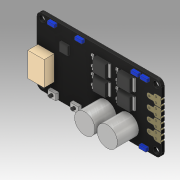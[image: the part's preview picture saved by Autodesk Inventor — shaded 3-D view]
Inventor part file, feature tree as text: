
AUTODESK INVENTOR PART (.ipt)
format: ipt  version: 2019.3 (Build 233278000, 278)  size: 836,096 bytes
history: native  units: mm
features: projected_geometry x23, extrude x14, sketch x14
ambient origin geometry x8: Origin, YZ Plane, XZ Plane, XY Plane, X Axis, Y Axis, Z Axis, Center Point
bodies: Solid1 (feature_tree)
feature tree (51):
  extrude  "Extrusion1"  Depth=33.0mm
  extrude  "Extrusion2"  Depth=3.0mm
  extrude  "Extrusion3"  Depth=28.0mm
  extrude  "Extrusion4"  Depth=10.0mm
  extrude  "Extrusion5"  Depth=21.0mm
  extrude  "Extrusion6"  Depth=10.5mm TaperAngle=0.0deg
  extrude  "Extrusion7"  Depth=6.0mm
  extrude  "Extrusion8"  Depth=4.5mm
  extrude  "Extrusion9"  Depth=2.1mm TaperAngle=0.0deg
  extrude  "Extrusion10"  Depth=0.6mm TaperAngle=0.0deg
  extrude  "Extrusion11"  Depth=2.5mm
  extrude  "Extrusion12"  Depth=3.5mm
  extrude  "Extrusion13"  Depth=5.5mm
  extrude  "Extrusion14"  Depth=0.25mm
  sketch  "Sketch1"  dims[d0=61.0mm d1=33.0mm]
  sketch  "Sketch2"  dims[d2=2.5mm d3=3.0mm]
  projected_geometry  "Projected Loop1"
  sketch  "Sketch3"  dims[d4=56.0mm d5=28.0mm]
  projected_geometry  "Projected Loop2"
  sketch  "Sketch4"  dims[d6=1.6mm d7=0.0mm d8=10.0mm]
  projected_geometry  "Projected Loop3"
  projected_geometry  "Projected Loop4"
  projected_geometry  "Projected Loop5"
  projected_geometry  "Projected Loop6"
  projected_geometry  "Projected Loop7"
  sketch  "Sketch5"  dims[d9=21.0mm d10=21.0mm]
  projected_geometry  "Projected Loop8"
  projected_geometry  "Projected Loop9"
  projected_geometry  "Projected Loop10"
  projected_geometry  "Projected Loop11"
  sketch  "Sketch6"  dims[d11=11.0mm d12=10.5mm d13=0.0mm]
  projected_geometry  "Projected Loop12"
  projected_geometry  "Projected Loop13"
  projected_geometry  "Projected Loop14"
  projected_geometry  "Projected Loop15"
  sketch  "Sketch7"  dims[d14=6.0mm d15=6.0mm]
  sketch  "Sketch8"  dims[d16=2.0mm d17=4.5mm]
  sketch  "Sketch9"  dims[d18=13.5mm d19=2.1mm d20=0.0mm]
  sketch  "Sketch10"  dims[d21=1.0mm d22=0.6mm d23=0.0mm]
  projected_geometry  "Projected Loop16"
  projected_geometry  "Projected Loop17"
  sketch  "Sketch11"  dims[d24=1.0mm d25=2.5mm]
  sketch  "Sketch12"  dims[d26=3.5mm d27=3.5mm]
  projected_geometry  "Projected Loop18"
  sketch  "Sketch13"  dims[d28=6.0mm d29=5.5mm]
  projected_geometry  "Projected Loop19"
  sketch  "Sketch14"  dims[d30=0.25mm d31=0.25mm d32=1.7mm d33=0.0mm d34=0.5mm d35=0.5mm d36=0.5mm d37=0.8mm d39=0.8mm d40=1.7mm d41=0.0mm d42=0.5mm d43=0.5mm d44=0.5mm d45=0.8mm d46=0.8mm d47=3.5mm d48=1.5mm d49=10.0mm d52=6.5mm d54=6.0mm d55=0.777816mm d56=0.5mm d57=1.0mm d58=5.5mm d59=1.0mm d60=1.5mm d61=0.0mm d62=12.0mm d63=8.0mm d64=0.5mm d65=14.3mm d66=5.0mm d67=0.0mm d68=4.0mm d69=4.0mm d70=3.0mm d71=7.0mm d72=6.8mm d73=0.5mm d74=1.5mm d75=0.0mm d76=1.5mm d77=1.0mm d78=0.0mm d79=4.0mm d80=4.0mm d81=7.0mm d82=12.0mm d83=1.0mm d84=0.0mm d85=0.8mm d86=80.0mm d88=2.54mm d89=20.0mm d91=2.54mm d94=7.61mm d95=7.61mm d96=40.0mm d98=5.08mm d99=10.0mm d101=10.0mm d103=1.27mm d104=3.3mm d105=1.0mm d106=0.0mm d111=4.9mm d112=2.5mm d113=40.0mm d115=5.08mm d116=10.0mm d118=10.0mm d120=0.01mm d121=0.0mm d122=0.01mm d123=0.0mm]
  projected_geometry  "Projected Loop20"
  projected_geometry  "Projected Loop21"
  projected_geometry  "Projected Loop22"
  projected_geometry  "Projected Loop23"
